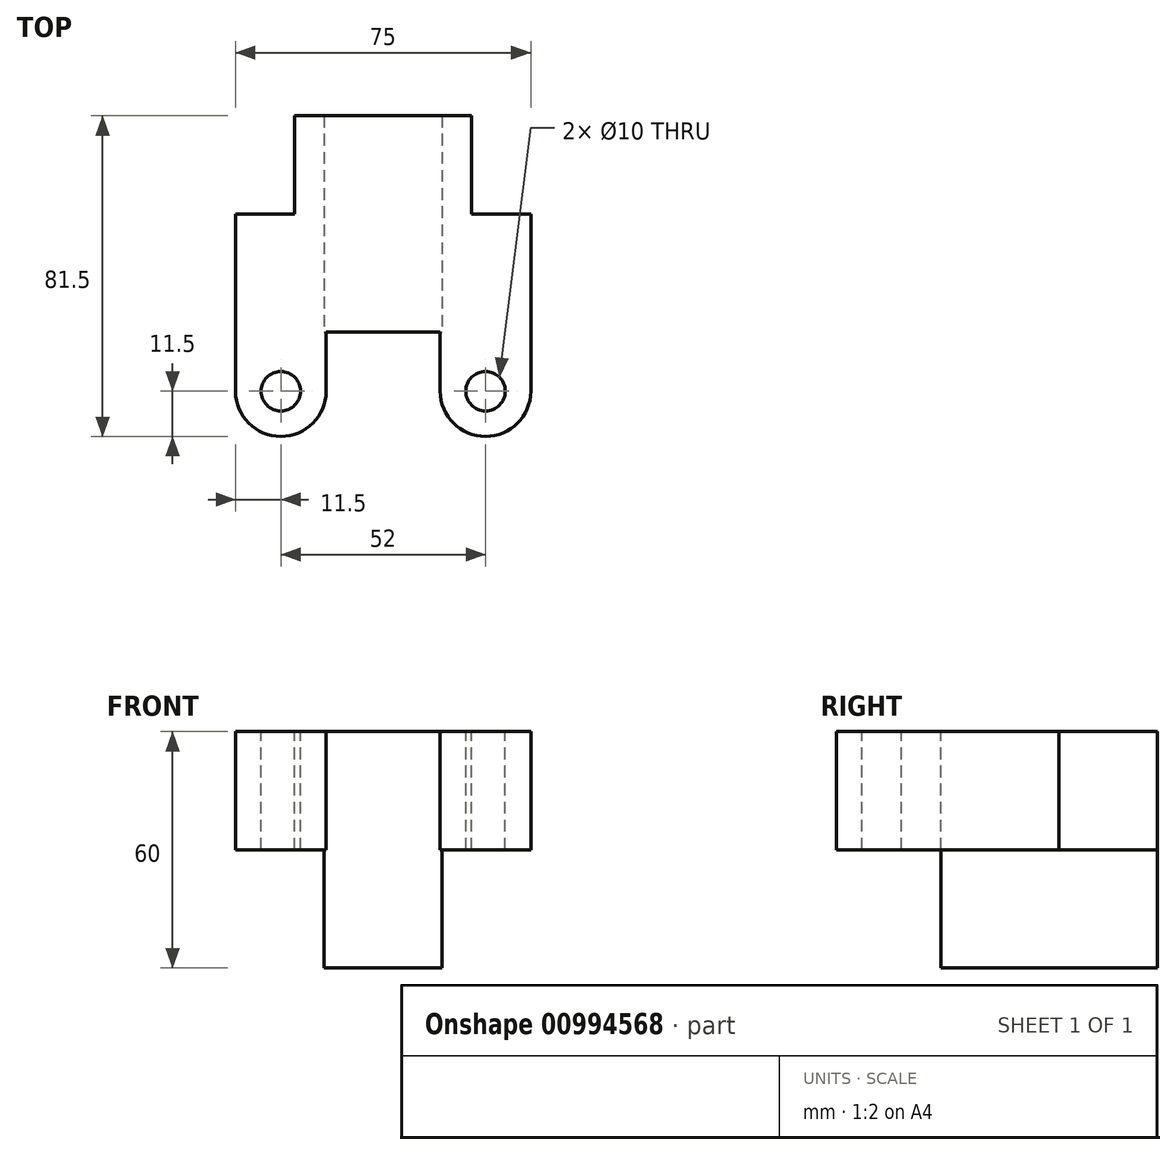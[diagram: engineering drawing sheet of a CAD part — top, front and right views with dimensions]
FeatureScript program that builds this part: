
annotation { "Feature Type Name" : "Feature", "Feature Type Description" : "" }
export const myFeature = defineFeature(function(context is Context, id is Id, definition is map)
    precondition{}
    {
        {
            var Q0;
            Q0=qCreatedBy(makeId("Front.planeOp"),FACE);
            var sketch = newSketch(context, id + "F0", { "sketchPlane" : qUnion([Q0])});
            skLineSegment(sketch, "E0", {"start": v(-37.5, 0) * mm, "end": v(-15, 0) * mm});
            skLineSegment(sketch, "E1", {"start": v(-15, 0) * mm, "end": v(-15, -30) * mm});
            skLineSegment(sketch, "E2", {"start": v(-15, -30) * mm, "end": v(0, -30) * mm});
            skLineSegment(sketch, "E3", {"start": v(0, 30) * mm, "end": v(-37.5, 30) * mm});
            skLineSegment(sketch, "E4", {"start": v(-37.5, 30) * mm, "end": v(-37.5, 0) * mm});
            skLineSegment(sketch, "E5.MirrorCS", {"start": v(37.5, 30) * mm, "end": v(37.5, 0) * mm});
            skLineSegment(sketch, "E6.MirrorCS", {"start": v(15, -30) * mm, "end": v(0, -30) * mm});
            skLineSegment(sketch, "E7.MirrorCS", {"start": v(0, 30) * mm, "end": v(37.5, 30) * mm});
            skLineSegment(sketch, "E8.MirrorCS", {"start": v(37.5, 0) * mm, "end": v(15, 0) * mm});
            skLineSegment(sketch, "E9.MirrorCS", {"start": v(15, 0) * mm, "end": v(15, -30) * mm});
            skSolve(sketch);
        }
        {
            var Q0;
            Q0=makeQuery(id+"F0.imprint","IMPRINT",FACE,{"disambiguationData":[TD([[makeQuery(id+"F0.imprint","IMPRINT",EDGE,{"derivedFrom":sQuery(id+"F0.wireOp",EDGE,"E0")}),1.0]])]});
            extrude(context, id + "F1", {"entities" : qUnion([Q0]), "oppositeDirection" : true, "depth" : 55 * mm, "offsetDistance" : 25 * mm});
        }
        {
            var Q0;
            Q0=makeQuery(id+"F1.opExtrude","SWEPT_FACE",FACE,{"disambiguationData":[OSD([sQuery(id+"F0.wireOp",EDGE,"E3"),sQuery(id+"F0.wireOp",EDGE,"E7.MirrorCS")])]});
            var sketch = newSketch(context, id + "F2", { "sketchPlane" : qUnion([Q0])});
            skLineSegment(sketch, "E10", {"start": v(0, 0) * mm, "end": v(-37.5, 0) * mm});
            skLineSegment(sketch, "E11", {"start": v(-37.5, 0) * mm, "end": v(-37.5, 30) * mm});
            skLineSegment(sketch, "E12", {"start": v(-22.5, 30) * mm, "end": v(-22.5, 55) * mm});
            skLineSegment(sketch, "E13", {"start": v(-22.5, 55) * mm, "end": v(0, 55) * mm});
            skLineSegment(sketch, "E14", {"start": v(-37.5, 30) * mm, "end": v(-22.5, 30) * mm});
            skLineSegment(sketch, "E15.MirrorCS", {"start": v(37.5, 30) * mm, "end": v(22.5, 30) * mm});
            skLineSegment(sketch, "E16.MirrorCS", {"start": v(0, 0) * mm, "end": v(37.5, 0) * mm});
            skLineSegment(sketch, "E17.MirrorCS", {"start": v(22.5, 55) * mm, "end": v(0, 55) * mm});
            skLineSegment(sketch, "E18.MirrorCS", {"start": v(37.5, 0) * mm, "end": v(37.5, 30) * mm});
            skLineSegment(sketch, "E19.MirrorCS", {"start": v(22.5, 30) * mm, "end": v(22.5, 55) * mm});
            skSolve(sketch);
        }
        {
            var Q0;
            {var subQ0=sQuery(id+"F2.wireOp",EDGE,"E12");Q0=makeQuery(id+"F2.imprint","IMPRINT",FACE,{"disambiguationData":[TD([[makeQuery(id+"F2.imprint","IMPRINT",EDGE,{"derivedFrom":subQ0}),1.0]])]});}
            var Q1;
            {var subQ0=sQuery(id+"F2.wireOp",EDGE,"E15.MirrorCS");Q1=makeQuery(id+"F2.imprint","IMPRINT",FACE,{"disambiguationData":[TD([[makeQuery(id+"F2.imprint","IMPRINT",EDGE,{"derivedFrom":subQ0}),-1.0]])]});}
            extrude(context, id + "F3", {"entities" : qUnion([Q0, Q1]), "operationType" : NewBodyOperationType.REMOVE, "oppositeDirection" : true, "depth" : 57.6 * mm, "offsetDistance" : 25 * mm});
        }
        {
            var Q0;
            Q0=makeQuery(id+"F1.opExtrude","SWEPT_FACE",FACE,{"disambiguationData":[OSD([sQuery(id+"F0.wireOp",EDGE,"E3"),sQuery(id+"F0.wireOp",EDGE,"E7.MirrorCS")])]});
            var sketch = newSketch(context, id + "F4", { "sketchPlane" : qUnion([Q0])});
            skLineSegment(sketch, "E20.bottom", {"start": v(-37.5, 0) * mm, "end": v(-14.5, 0) * mm});
            skLineSegment(sketch, "E20.left", {"start": v(-37.5, 0) * mm, "end": v(-37.5, -15) * mm});
            skLineSegment(sketch, "E20.right", {"start": v(-14.5, 0) * mm, "end": v(-14.5, -15) * mm});
            skArc(sketch, "E21", {"start": v(-37.5, -15) * mm, "mid": v(-26, -26.5) * mm, "end": v(-14.5, -15) * mm});
            skCircle(sketch, "E22", {"center": v(-26, -15) * mm, "radius": 5 * mm});
            skLineSegment(sketch, "E23.MirrorCS", {"start": v(14.5, 0) * mm, "end": v(14.5, -15) * mm});
            skLineSegment(sketch, "E24.MirrorCS", {"start": v(37.5, 0) * mm, "end": v(37.5, -15) * mm});
            skLineSegment(sketch, "E25.MirrorCS", {"start": v(37.5, 0) * mm, "end": v(14.5, 0) * mm});
            skCircle(sketch, "E26.MirrorC", {"center": v(26, -15) * mm, "radius": 5 * mm});
            skArc(sketch, "E27.MirrorCS", {"start": v(37.5, -15) * mm, "mid": v(26, -26.5) * mm, "end": v(14.5, -15) * mm});
            skSolve(sketch);
        }
        {
            var Q0;
            Q0=makeQuery(id+"F4.imprint","IMPRINT",FACE,{"disambiguationData":[TD([[makeQuery(id+"F4.imprint","IMPRINT",EDGE,{"derivedFrom":sQuery(id+"F4.wireOp",EDGE,"E20.bottom")}),-1.0]])]});
            var Q1;
            Q1=makeQuery(id+"F4.imprint","IMPRINT",FACE,{"disambiguationData":[TD([[makeQuery(id+"F4.imprint","IMPRINT",EDGE,{"derivedFrom":sQuery(id+"F4.wireOp",EDGE,"E23.MirrorCS")}),1.0]])]});
            extrude(context, id + "F5", {"entities" : qUnion([Q0, Q1]), "operationType" : NewBodyOperationType.ADD, "oppositeDirection" : true, "depth" : 30 * mm, "offsetDistance" : 25 * mm});
        }
    });
